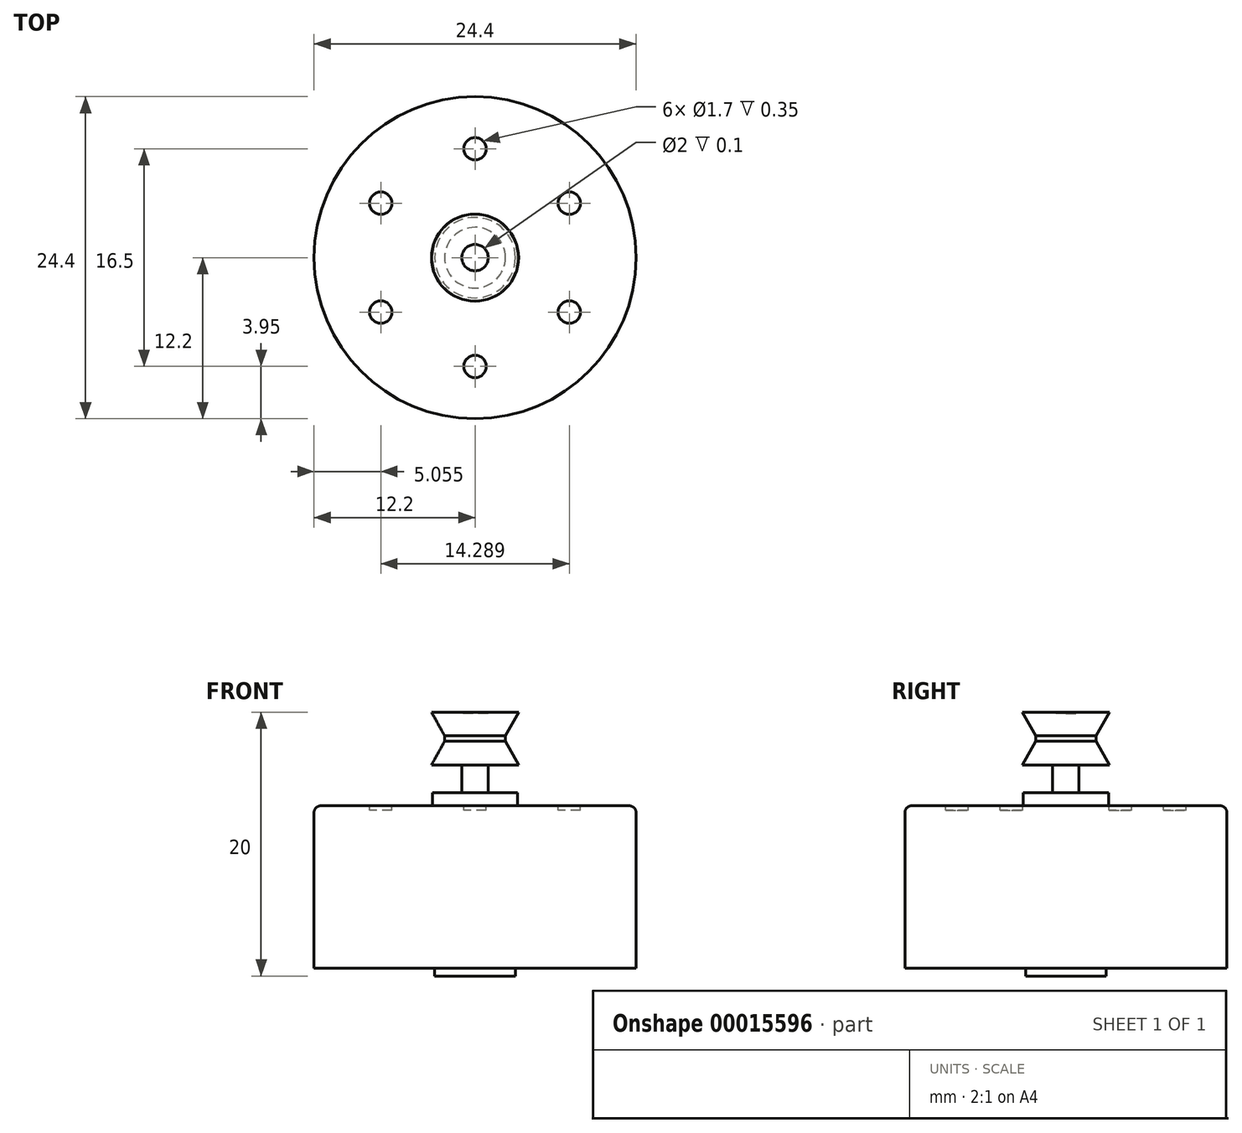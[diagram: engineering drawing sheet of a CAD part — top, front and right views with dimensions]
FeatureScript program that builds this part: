
annotation { "Feature Type Name" : "Feature", "Feature Type Description" : "" }
export const myFeature = defineFeature(function(context is Context, id is Id, definition is map)
    precondition{}
    {
        {
            var Q0;
            Q0=qCreatedBy(makeId("Top.planeOp"),FACE);
            var sketch = newSketch(context, id + "F0", { "sketchPlane" : qUnion([Q0])});
            skCircle(sketch, "E0", {"center": v(0, 0) * mm, "radius": 12.2 * mm});
            skSolve(sketch);
        }
        {
            var Q0;
            Q0=makeQuery(id+"F0.imprint","IMPRINT",FACE,{"disambiguationData":[TD([[makeQuery(id+"F0.imprint","IMPRINT",EDGE,{"derivedFrom":sQuery(id+"F0.wireOp",EDGE,"E0")}),1.0]])]});
            extrude(context, id + "F1", {"entities" : qUnion([Q0]), "oppositeDirection" : true, "depth" : 12.3 * mm});
        }
        {
            var Q0;
            Q0=makeQuery(id+"F1.opExtrude","CAP_FACE",FACE,{"disambiguationData":[OSD([sQuery(id+"F0.wireOp",EDGE,"E0")])],"isStart":true});
            var sketch = newSketch(context, id + "F2", { "sketchPlane" : qUnion([Q0])});
            skCircle(sketch, "E1", {"center": v(0, 0) * mm, "radius": 3.23 * mm});
            skSolve(sketch);
        }
        {
            var Q0;
            Q0=makeQuery(id+"F2.imprint","IMPRINT",FACE,{"disambiguationData":[TD([[makeQuery(id+"F2.imprint","IMPRINT",EDGE,{"derivedFrom":sQuery(id+"F2.wireOp",EDGE,"E1")}),1.0]])]});
            extrude(context, id + "F3", {"entities" : qUnion([Q0]), "operationType" : NewBodyOperationType.ADD, "depth" : 1 * mm});
        }
        {
            var Q0;
            Q0=makeQuery(id+"F1.opExtrude","CAP_FACE",FACE,{"disambiguationData":[OSD([sQuery(id+"F0.wireOp",EDGE,"E0")])],"isStart":false});
            var sketch = newSketch(context, id + "F4", { "sketchPlane" : qUnion([Q0])});
            skCircle(sketch, "E2", {"center": v(0, 0) * mm, "radius": 3.05 * mm});
            skSolve(sketch);
        }
        {
            var Q0;
            Q0=makeQuery(id+"F4.imprint","IMPRINT",FACE,{"disambiguationData":[TD([[makeQuery(id+"F4.imprint","IMPRINT",EDGE,{"derivedFrom":sQuery(id+"F4.wireOp",EDGE,"E2")}),1.0]])]});
            extrude(context, id + "F5", {"entities" : qUnion([Q0]), "operationType" : NewBodyOperationType.ADD, "depth" : 0.6 * mm});
        }
        {
            var Q0;
            Q0=makeQuery(id+"F3.opExtrude","CAP_FACE",FACE,{"disambiguationData":[OSD([sQuery(id+"F2.wireOp",EDGE,"E1")])],"isStart":false});
            var sketch = newSketch(context, id + "F6", { "sketchPlane" : qUnion([Q0])});
            skCircle(sketch, "E3", {"center": v(0, 0) * mm, "radius": 1 * mm});
            skSolve(sketch);
        }
        {
            var Q0;
            Q0=makeQuery(id+"F6.imprint","IMPRINT",FACE,{"disambiguationData":[TD([[makeQuery(id+"F6.imprint","IMPRINT",EDGE,{"derivedFrom":sQuery(id+"F6.wireOp",EDGE,"E3")}),1.0]])]});
            extrude(context, id + "F7", {"entities" : qUnion([Q0]), "depth" : 6 * mm});
        }
        {
            var Q0;
            Q0=makeQuery(id+"F1.opExtrude","CAP_FACE",FACE,{"disambiguationData":[OSD([sQuery(id+"F0.wireOp",EDGE,"E0")])],"isStart":true});
            var sketch = newSketch(context, id + "F8", { "sketchPlane" : qUnion([Q0])});
            skCircle(sketch, "E4", {"center": v(0, 8.25) * mm, "radius": 0.85 * mm});
            skCircle(sketch, "E5.1.0", {"center": v(-7.14, 4.13) * mm, "radius": 0.85 * mm});
            skCircle(sketch, "E5.2.0", {"center": v(-7.14, -4.12) * mm, "radius": 0.85 * mm});
            skCircle(sketch, "E5.3.0", {"center": v(0, -8.25) * mm, "radius": 0.85 * mm});
            skCircle(sketch, "E5.4.0", {"center": v(7.14, -4.13) * mm, "radius": 0.85 * mm});
            skCircle(sketch, "E5.5.0", {"center": v(7.14, 4.13) * mm, "radius": 0.85 * mm});
            skPoint(sketch, "E5.center", {"position": v(0, 0) * mm});
            skSolve(sketch);
        }
        {
            var Q0;
            Q0=makeQuery(id+"F8.imprint","IMPRINT",FACE,{"disambiguationData":[TD([[makeQuery(id+"F8.imprint","IMPRINT",EDGE,{"derivedFrom":sQuery(id+"F8.wireOp",EDGE,"E4")}),1.0]])]});
            var Q1;
            Q1=makeQuery(id+"F8.imprint","IMPRINT",FACE,{"disambiguationData":[TD([[makeQuery(id+"F8.imprint","IMPRINT",EDGE,{"derivedFrom":sQuery(id+"F8.wireOp",EDGE,"E5.5.0")}),1.0]])]});
            var Q2;
            Q2=makeQuery(id+"F8.imprint","IMPRINT",FACE,{"disambiguationData":[TD([[makeQuery(id+"F8.imprint","IMPRINT",EDGE,{"derivedFrom":sQuery(id+"F8.wireOp",EDGE,"E5.4.0")}),1.0]])]});
            var Q3;
            Q3=makeQuery(id+"F8.imprint","IMPRINT",FACE,{"disambiguationData":[TD([[makeQuery(id+"F8.imprint","IMPRINT",EDGE,{"derivedFrom":sQuery(id+"F8.wireOp",EDGE,"E5.3.0")}),1.0]])]});
            var Q4;
            Q4=makeQuery(id+"F8.imprint","IMPRINT",FACE,{"disambiguationData":[TD([[makeQuery(id+"F8.imprint","IMPRINT",EDGE,{"derivedFrom":sQuery(id+"F8.wireOp",EDGE,"E5.2.0")}),1.0]])]});
            var Q5;
            Q5=makeQuery(id+"F8.imprint","IMPRINT",FACE,{"disambiguationData":[TD([[makeQuery(id+"F8.imprint","IMPRINT",EDGE,{"derivedFrom":sQuery(id+"F8.wireOp",EDGE,"E5.1.0")}),1.0]])]});
            extrude(context, id + "F9", {"entities" : qUnion([Q0, Q1, Q2, Q3, Q4, Q5]), "operationType" : NewBodyOperationType.REMOVE, "oppositeDirection" : true, "depth" : 0.35 * mm});
        }
        {
            var Q0;
            Q0=makeQuery(id+"F1.opExtrude","CAP_EDGE",EDGE,{"disambiguationData":[OSD([sQuery(id+"F0.wireOp",EDGE,"E0")])],"isStart":true});
            fillet(context, id + "F10", {"entities" : qUnion([Q0]), "radius" : 0.5 * mm, "tangentPropagation" : true, "allowEdgeOverflow" : false});
        }
        {
            var Q0;
            Q0=qCreatedBy(makeId("Front.planeOp"),FACE);
            var sketch = newSketch(context, id + "F11", { "sketchPlane" : qUnion([Q0])});
            skLineSegment(sketch, "E6.0", {"start": v(-1, 7) * mm, "end": v(1, 7) * mm, "construction": true});
            skLineSegment(sketch, "E7.0", {"start": v(-1, 1) * mm, "end": v(1, 1) * mm, "construction": true});
            skLineSegment(sketch, "E8", {"start": v(-1, 7) * mm, "end": v(-1, 1) * mm, "construction": true});
            skLineSegment(sketch, "E9.bottom", {"start": v(-1, 5.1) * mm, "end": v(-3.3, 5.1) * mm});
            skLineSegment(sketch, "E9.top", {"start": v(-1, 7.1) * mm, "end": v(-3.3, 7.1) * mm});
            skLineSegment(sketch, "E9.left", {"start": v(-1, 5.1) * mm, "end": v(-1, 7.1) * mm});
            skLineSegment(sketch, "E9.right", {"start": v(-3.3, 5.1) * mm, "end": v(-3.3, 7.1) * mm});
            skPoint(sketch, "E10", {"position": v(0, 7) * mm});
            skPoint(sketch, "E11", {"position": v(-2.3, 5.1) * mm});
            skLineSegment(sketch, "E12", {"start": v(-2.3, 5.1) * mm, "end": v(-2.3, 5.3) * mm});
            skLineSegment(sketch, "E13", {"start": v(-2.3, 5.3) * mm, "end": v(-3.3, 7.1) * mm});
            skSolve(sketch);
        }
        {
            var Q0;
            {var subQ5=sQuery(id+"F11.wireOp",EDGE,"E9.top");Q0=makeQuery(id+"F11.imprint","IMPRINT",FACE,{"disambiguationData":[TD([[makeQuery(id+"F11.imprint","IMPRINT",EDGE,{"derivedFrom":subQ5}),1.0]])]});}
            var Q1;
            Q1=makeQuery(id+"F7.opExtrude","CAP_EDGE",EDGE,{"disambiguationData":[OSD([sQuery(id+"F6.wireOp",EDGE,"E3")])],"isStart":false});
            revolve(context, id + "F12", {"entities" : qUnion([Q0]), "axis" : qUnion([Q1]), "revolveType" : RevolveType.FULL});
        }
        {
            var Q0;
            Q0=makeQuery(id+"F12.opRevolve","SWEPT_BODY",BODY,{"disambiguationData":[OSD([sQuery(id+"F11.wireOp",EDGE,"E9.bottom"),sQuery(id+"F11.wireOp",EDGE,"E9.top"),sQuery(id+"F11.wireOp",EDGE,"E9.left"),sQuery(id+"F11.wireOp",EDGE,"E9.right"),sQuery(id+"F11.wireOp",EDGE,"2485923f-37fa-4326-9059-831a4d72c2a7")])]});
            var Q1;
            Q1=makeQuery(id+"F12.opRevolve","SWEPT_FACE",FACE,{"disambiguationData":[OSD([sQuery(id+"F11.wireOp",EDGE,"E9.bottom")])]});
            mirror(context, id + "F13", {"operationType" : NewBodyOperationType.ADD, "entities" : qUnion([Q0]), "mirrorPlane" : qUnion([Q1])});
        }
    });
